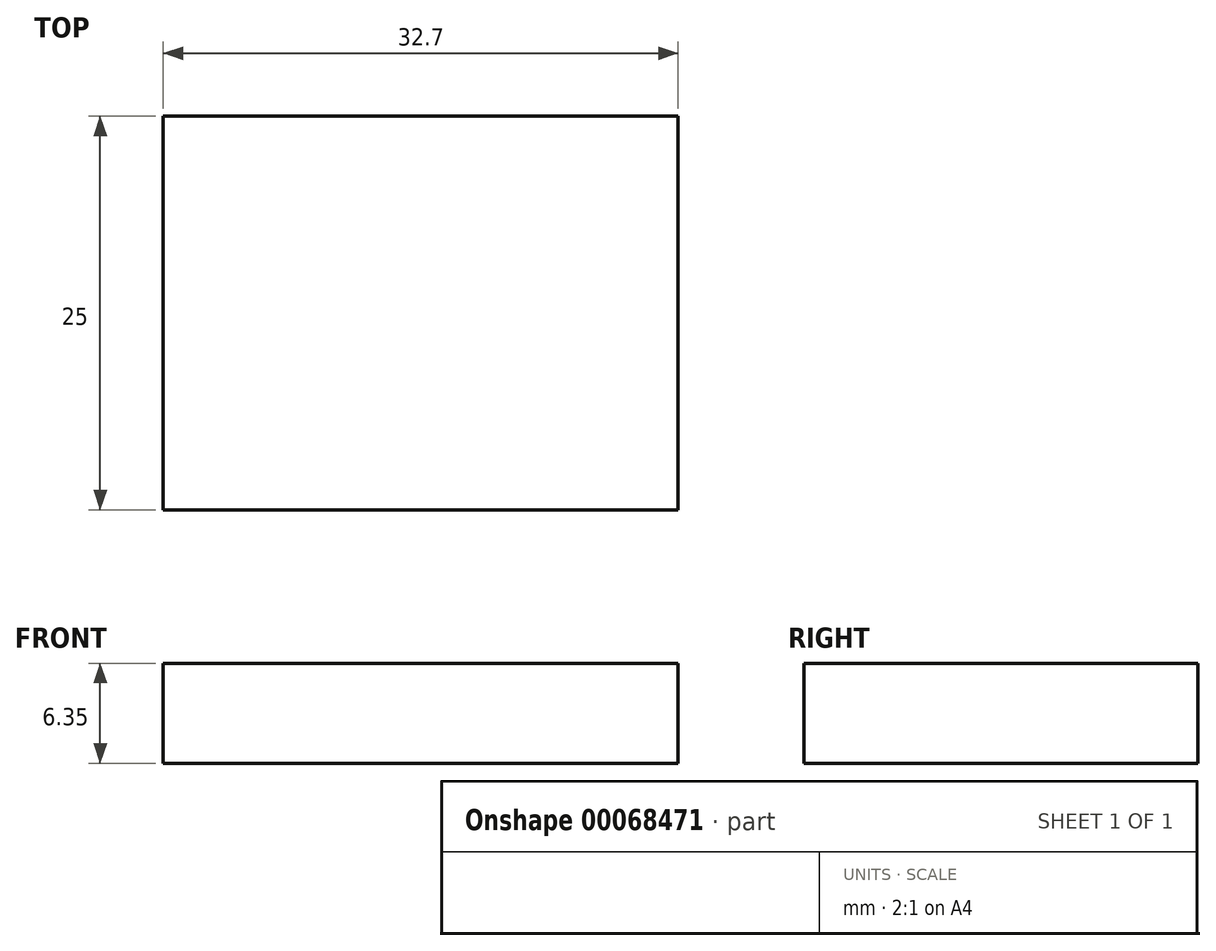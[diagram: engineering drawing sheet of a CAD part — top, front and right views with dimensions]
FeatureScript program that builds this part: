
annotation { "Feature Type Name" : "Feature", "Feature Type Description" : "" }
export const myFeature = defineFeature(function(context is Context, id is Id, definition is map)
    precondition{}
    {
        {
            var Q0;
            Q0=qCreatedBy(makeId("Top.planeOp"),FACE);
            var sketch = newSketch(context, id + "F0", { "sketchPlane" : qUnion([Q0])});
            skLineSegment(sketch, "E0.rect.bottom", {"start": v(16.35, 12.5) * mm, "end": v(-16.35, 12.5) * mm});
            skLineSegment(sketch, "E0.rect.top", {"start": v(16.35, -12.5) * mm, "end": v(-16.35, -12.5) * mm});
            skLineSegment(sketch, "E0.rect.left", {"start": v(16.35, 12.5) * mm, "end": v(16.35, -12.5) * mm});
            skLineSegment(sketch, "E0.rect.right", {"start": v(-16.35, 12.5) * mm, "end": v(-16.35, -12.5) * mm});
            skPoint(sketch, "E0.rect.middle", {"position": v(0, 0) * mm});
            skSolve(sketch);
        }
        {
            var Q0;
            Q0 = qSketchRegion(id + "F0", true);
            extrude(context, id + "F1", {"entities" : qUnion([Q0]), "depth" : 6.35 * mm});
        }
    });
